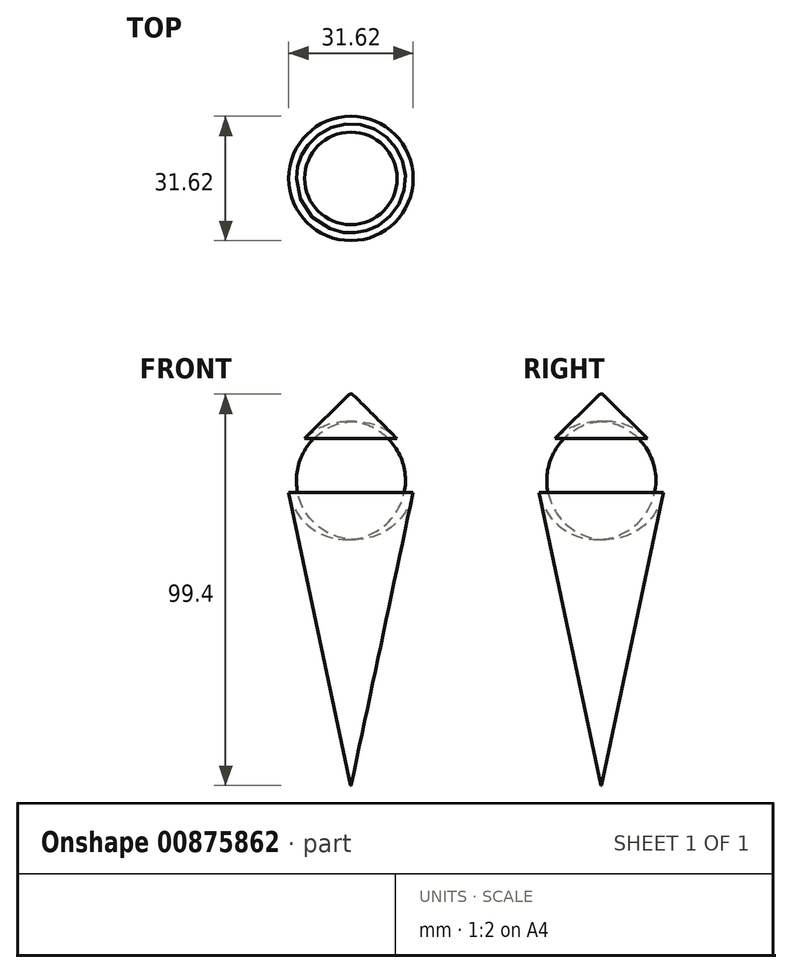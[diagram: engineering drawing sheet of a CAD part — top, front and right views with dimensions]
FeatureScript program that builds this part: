
annotation { "Feature Type Name" : "Feature", "Feature Type Description" : "" }
export const myFeature = defineFeature(function(context is Context, id is Id, definition is map)
    precondition{}
    {
        {
            var Q0;
            Q0=qCreatedBy(makeId("Front.planeOp"),FACE);
            var sketch = newSketch(context, id + "F0", { "sketchPlane" : qUnion([Q0])});
            skLineSegment(sketch, "E0", {"start": v(-0.05, 0.23) * mm, "end": v(-17.5, 82.5) * mm});
            skLineSegment(sketch, "E1", {"start": v(-17.5, 82.5) * mm, "end": v(-0.7, 99.3) * mm});
            skLineSegment(sketch, "E2", {"start": v(0, 99.59) * mm, "end": v(0, 0.2) * mm});
            skArc(sketch, "E3", {"start": v(0, 99.59) * mm, "mid": v(-0.38, 99.5) * mm, "end": v(-0.7, 99.3) * mm});
            skPoint(sketch, "E4.orphan", {"position": v(0, 100) * mm});
            skArc(sketch, "E5", {"start": v(-0.05, 0.23) * mm, "mid": v(-0.03, 0.2) * mm, "end": v(0, 0.2) * mm});
            skPoint(sketch, "E6.orphan", {"position": v(0, 0) * mm});
            skSolve(sketch);
        }
        {
            var Q0;
            Q0 = qSketchRegion(id + "F0", true);
            var Q1;
            Q1=sQuery(id+"F0.wireOp",EDGE,"E2");
            revolve(context, id + "F1", {"surfaceOperationType" : NewSurfaceOperationType.NEW, "entities" : qUnion([Q0]), "axis" : qUnion([Q1]), "revolveType" : RevolveType.FULL});
        }
        {
            var Q0;
            Q0=makeQuery(id+"F1.opRevolve","SWEPT_EDGE",EDGE,{"disambiguationData":[OSD([sQuery(id+"F0.wireOp",EDGE,"E0"),sQuery(id+"F0.wireOp",EDGE,"E1")])]});
            fillet(context, id + "F2", {"entities" : qUnion([Q0]), "radius" : 15 * mm, "tangentPropagation" : true, "allowEdgeOverflow" : false});
        }
    });
